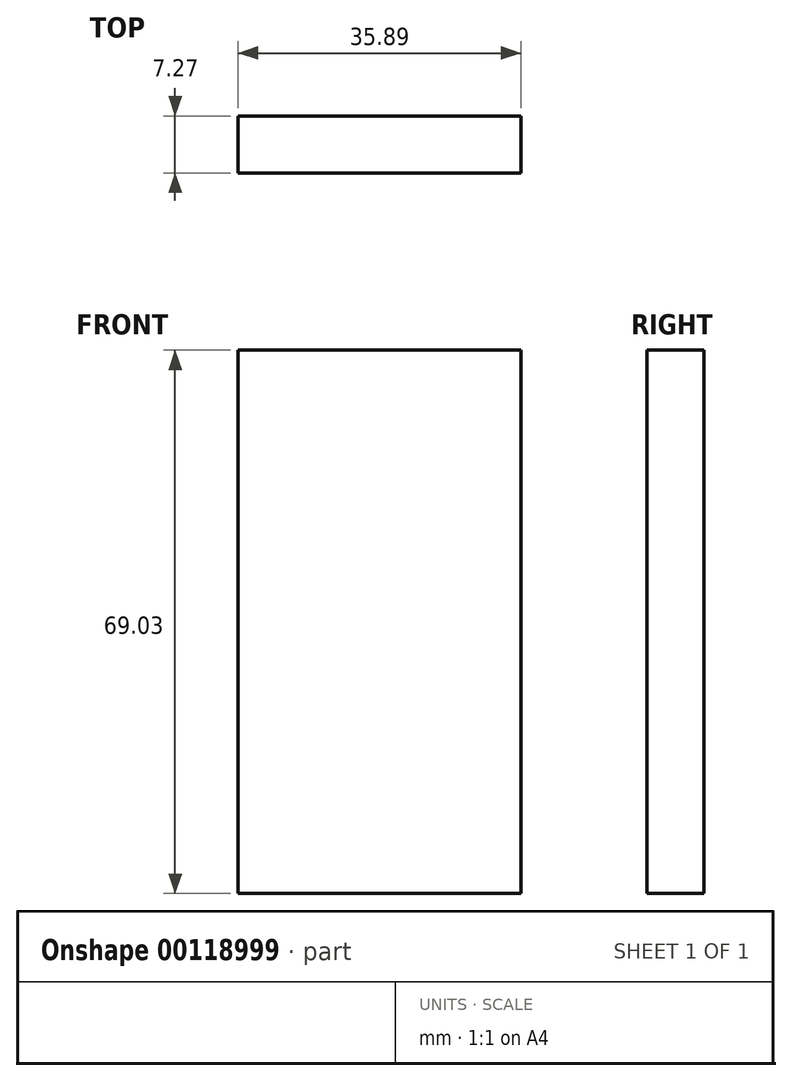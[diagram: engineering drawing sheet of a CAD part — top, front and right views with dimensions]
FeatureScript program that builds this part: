
annotation { "Feature Type Name" : "Feature", "Feature Type Description" : "" }
export const myFeature = defineFeature(function(context is Context, id is Id, definition is map)
    precondition{}
    {
        {
            var Q0;
            Q0=qCreatedBy(makeId("Front.planeOp"),FACE);
            var sketch = newSketch(context, id + "F0", { "sketchPlane" : qUnion([Q0])});
            skLineSegment(sketch, "E0.bottom", {"start": v(0, 0) * mm, "end": v(35.89, 0) * mm});
            skLineSegment(sketch, "E0.top", {"start": v(0, 69.03) * mm, "end": v(35.89, 69.03) * mm});
            skLineSegment(sketch, "E0.left", {"start": v(0, 0) * mm, "end": v(0, 69.03) * mm});
            skLineSegment(sketch, "E0.right", {"start": v(35.89, 0) * mm, "end": v(35.89, 69.03) * mm});
            skSolve(sketch);
        }
        {
            var Q0;
            Q0 = qSketchRegion(id + "F0", true);
            extrude(context, id + "F1", {"entities" : qUnion([Q0]), "depth" : 7.27 * mm});
        }
    });
